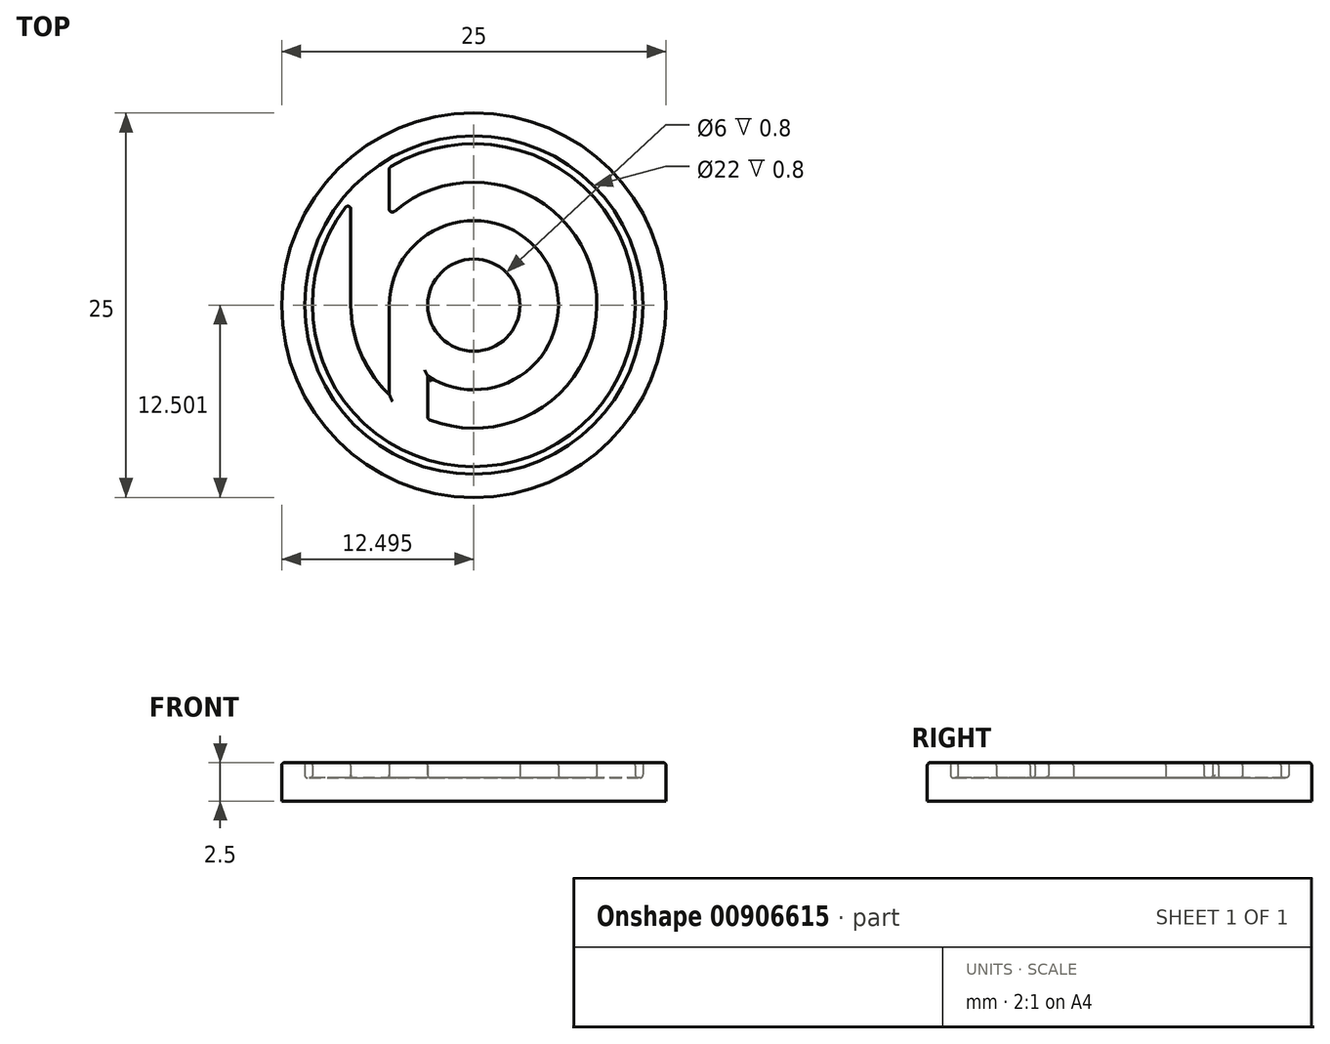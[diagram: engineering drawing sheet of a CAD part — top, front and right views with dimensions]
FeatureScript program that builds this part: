
annotation { "Feature Type Name" : "Feature", "Feature Type Description" : "" }
export const myFeature = defineFeature(function(context is Context, id is Id, definition is map)
    precondition{}
    {
        {
            var Q0;
            Q0=qCreatedBy(makeId("Top.planeOp"),FACE);
            var sketch = newSketch(context, id + "F0", { "sketchPlane" : qUnion([Q0])});
            skCircle(sketch, "E0", {"center": v(-249, 13.34) * mm, "radius": 3 * mm});
            skArc(sketch, "E1", {"start": v(-252, 8.73) * mm, "mid": v(-244.16, 15.96) * mm, "end": v(-254.5, 13.34) * mm});
            skArc(sketch, "E2", {"start": v(-257, 13.34) * mm, "mid": v(-256.34, 10.18) * mm, "end": v(-254.5, 7.53) * mm});
            skArc(sketch, "E3", {"start": v(-257, 20.14) * mm, "mid": v(-242.16, 5.37) * mm, "end": v(-254.5, 22.28) * mm});
            skCircle(sketch, "E4", {"center": v(-249, 13.34) * mm, "radius": 11 * mm});
            skCircle(sketch, "E5", {"center": v(-249, 13.34) * mm, "radius": 12.5 * mm});
            skLineSegment(sketch, "E6", {"start": v(-252, 8.73) * mm, "end": v(-252, 5.92) * mm});
            skLineSegment(sketch, "E7", {"start": v(-254.5, 13.34) * mm, "end": v(-254.5, 7.53) * mm});
            skPoint(sketch, "E8.orphan", {"position": v(-252, 13.34) * mm});
            skLineSegment(sketch, "E9", {"start": v(-257, 13.34) * mm, "end": v(-257, 20.14) * mm});
            skLineSegment(sketch, "E10", {"start": v(-254.5, 19.15) * mm, "end": v(-254.5, 22.28) * mm});
            skArc(sketch, "E11.trimOffspring", {"start": v(-252, 5.92) * mm, "mid": v(-241.13, 14.83) * mm, "end": v(-254.5, 19.15) * mm});
            skSolve(sketch);
        }
        {
            var Q0;
            Q0 = qSketchRegion(id + "F0", true);
            var Q1;
            Q1=makeQuery(id+"F0.imprint","IMPRINT",FACE,{"disambiguationData":[TD([[makeQuery(id+"F0.imprint","IMPRINT",EDGE,{"derivedFrom":sQuery(id+"F0.wireOp",EDGE,"E1")}),-1.0]])]});
            var Q2;
            Q2=makeQuery(id+"F0.imprint","IMPRINT",FACE,{"disambiguationData":[TD([[makeQuery(id+"F0.imprint","IMPRINT",EDGE,{"derivedFrom":sQuery(id+"F0.wireOp",EDGE,"E0")}),-1.0]])]});
            var Q3;
            Q3=makeQuery(id+"F0.imprint","IMPRINT",FACE,{"disambiguationData":[TD([[makeQuery(id+"F0.imprint","IMPRINT",EDGE,{"derivedFrom":sQuery(id+"F0.wireOp",EDGE,"E0")}),1.0]])]});
            extrude(context, id + "F1", {"entities" : qUnion([Q0, Q1, Q2, Q3]), "oppositeDirection" : true, "depth" : 1.5 * mm, "offsetDistance" : 25 * mm});
        }
        {
            var Q0;
            Q0 = qSketchRegion(id + "F0", true);
            var Q1;
            Q1=makeQuery(id+"F0.imprint","IMPRINT",FACE,{"disambiguationData":[TD([[makeQuery(id+"F0.imprint","IMPRINT",EDGE,{"derivedFrom":sQuery(id+"F0.wireOp",EDGE,"E0")}),-1.0]])]});
            extrude(context, id + "F2", {"entities" : qUnion([Q0, Q1]), "operationType" : NewBodyOperationType.ADD, "depth" : 1 * mm, "offsetDistance" : 25 * mm});
        }
        {
            var Q0;
            Q0=makeQuery(id+"F2.opExtrude","CAP_EDGE",EDGE,{"disambiguationData":[OSD([sQuery(id+"F0.wireOp",EDGE,"E5")])],"isStart":false});
            var Q1;
            Q1=makeQuery(id+"F2.opExtrude","CAP_EDGE",EDGE,{"disambiguationData":[OSD([sQuery(id+"F0.wireOp",EDGE,"E9")])],"isStart":false});
            var Q2;
            Q2=makeQuery(id+"F2.opExtrude","CAP_EDGE",EDGE,{"disambiguationData":[OSD([sQuery(id+"F0.wireOp",EDGE,"E2")])],"isStart":false});
            var Q3;
            Q3=makeQuery(id+"F2.opExtrude","CAP_EDGE",EDGE,{"disambiguationData":[OSD([sQuery(id+"F0.wireOp",EDGE,"E10")])],"isStart":false});
            var Q4;
            Q4=makeQuery(id+"F2.opExtrude","CAP_EDGE",EDGE,{"disambiguationData":[OSD([sQuery(id+"F0.wireOp",EDGE,"E7")])],"isStart":false});
            var Q5;
            Q5=makeQuery(id+"F2.opExtrude","CAP_EDGE",EDGE,{"disambiguationData":[OSD([sQuery(id+"F0.wireOp",EDGE,"E6")])],"isStart":false});
            var Q6;
            Q6=makeQuery(id+"F2.opExtrude","CAP_EDGE",EDGE,{"disambiguationData":[OSD([sQuery(id+"F0.wireOp",EDGE,"E0")])],"isStart":true});
            var Q7;
            Q7=makeQuery(id+"F2.opExtrude","CAP_EDGE",EDGE,{"disambiguationData":[OSD([sQuery(id+"F0.wireOp",EDGE,"E11.trimOffspring")])],"isStart":true});
            var Q8;
            Q8=makeQuery(id+"F2.opExtrude","CAP_EDGE",EDGE,{"disambiguationData":[OSD([sQuery(id+"F0.wireOp",EDGE,"E1")])],"isStart":true});
            var Q9;
            Q9=makeQuery(id+"F2.opExtrude","CAP_EDGE",EDGE,{"disambiguationData":[OSD([sQuery(id+"F0.wireOp",EDGE,"E7")])],"isStart":true});
            var Q10;
            Q10=makeQuery(id+"F2.opExtrude","CAP_EDGE",EDGE,{"disambiguationData":[OSD([sQuery(id+"F0.wireOp",EDGE,"E10")])],"isStart":true});
            var Q11;
            Q11=makeQuery(id+"F2.opExtrude","CAP_EDGE",EDGE,{"disambiguationData":[OSD([sQuery(id+"F0.wireOp",EDGE,"E4")])],"isStart":true});
            var Q12;
            Q12=makeQuery(id+"F2.opExtrude","CAP_EDGE",EDGE,{"disambiguationData":[OSD([sQuery(id+"F0.wireOp",EDGE,"E3")])],"isStart":true});
            var Q13;
            Q13=makeQuery(id+"F2.opExtrude","CAP_EDGE",EDGE,{"disambiguationData":[OSD([sQuery(id+"F0.wireOp",EDGE,"E0")])],"isStart":false});
            var Q14;
            Q14=makeQuery(id+"F2.opExtrude","CAP_EDGE",EDGE,{"disambiguationData":[OSD([sQuery(id+"F0.wireOp",EDGE,"E11.trimOffspring")])],"isStart":false});
            var Q15;
            Q15=makeQuery(id+"F2.opExtrude","CAP_EDGE",EDGE,{"disambiguationData":[OSD([sQuery(id+"F0.wireOp",EDGE,"E6")])],"isStart":true});
            var Q16;
            Q16=makeQuery(id+"F2.opExtrude","SWEPT_EDGE",EDGE,{"disambiguationData":[OSD([sQuery(id+"F0.wireOp",EDGE,"E6"),sQuery(id+"F0.wireOp",EDGE,"E11.trimOffspring")])]});
            var Q17;
            Q17=makeQuery(id+"F2.opExtrude","SWEPT_EDGE",EDGE,{"disambiguationData":[OSD([sQuery(id+"F0.wireOp",EDGE,"E10"),sQuery(id+"F0.wireOp",EDGE,"E11.trimOffspring")])]});
            var Q18;
            Q18=makeQuery(id+"F2.opExtrude","SWEPT_EDGE",EDGE,{"disambiguationData":[OSD([sQuery(id+"F0.wireOp",EDGE,"E3"),sQuery(id+"F0.wireOp",EDGE,"E10")])]});
            var Q19;
            Q19=makeQuery(id+"F2.opExtrude","SWEPT_EDGE",EDGE,{"disambiguationData":[OSD([sQuery(id+"F0.wireOp",EDGE,"E3"),sQuery(id+"F0.wireOp",EDGE,"E9")])]});
            var Q20;
            Q20=makeQuery(id+"F2.opExtrude","CAP_FACE",FACE,{"disambiguationData":[OSD([sQuery(id+"F0.wireOp",EDGE,"E0"),sQuery(id+"F0.wireOp",EDGE,"E1"),sQuery(id+"F0.wireOp",EDGE,"E2"),sQuery(id+"F0.wireOp",EDGE,"E3"),sQuery(id+"F0.wireOp",EDGE,"E6"),sQuery(id+"F0.wireOp",EDGE,"E7"),sQuery(id+"F0.wireOp",EDGE,"E9"),sQuery(id+"F0.wireOp",EDGE,"E10"),sQuery(id+"F0.wireOp",EDGE,"E11.trimOffspring")])],"isStart":false});
            fillet(context, id + "F3", {"entities" : qUnion([Q0, Q1, Q2, Q3, Q4, Q5, Q6, Q7, Q8, Q9, Q10, Q11, Q12, Q13, Q14, Q15, Q16, Q17, Q18, Q19, Q20]), "radius" : .2 * mm, "tangentPropagation" : true, "allowEdgeOverflow" : false});
        }
    });
